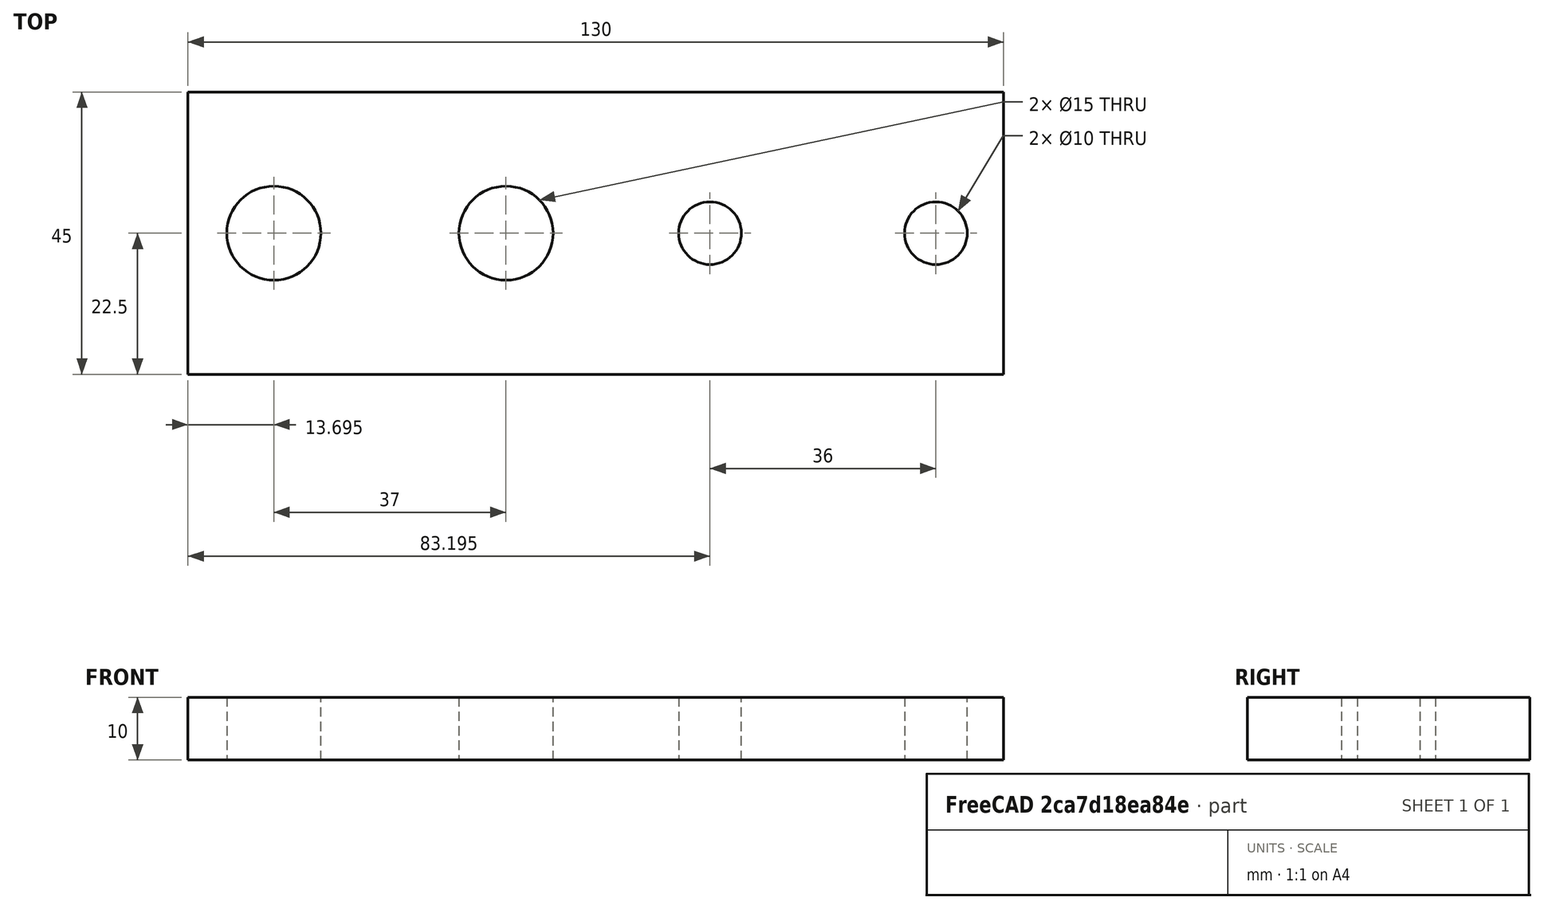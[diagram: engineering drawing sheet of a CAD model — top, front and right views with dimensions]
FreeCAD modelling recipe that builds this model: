
FCSTD DOCUMENT  (FreeCAD 2024.409R38991 (Git))
Label: SkadisMonkeyWrench
License: All rights reserved
LicenseURL: https://en.wikipedia.org/wiki/All_rights_reserved
objects: Sketcher::SketchObject×1, PartDesign::Pad×1, PartDesign::Body×1
note: 6 computed .brp shape members not serialized (recipe doc carries the construction recipe); baked Part::Feature solids carry a one-line shape summary decoded from their .brp

FEATURE [Sketcher::SketchObject] Sketch
  ArcFitTolerance = 1e-06
  AttachmentSupport = -> [XY_Plane]
  ExternalBSplineMaxDegree = 5
  ExternalBSplineTolerance = 0.0001
  FullyConstrained = false
  InternalTolerance = 1e-06
  InvalidShape = false
  MakeInternals = false
  MapMode = 5
  Support = -> [XY_Plane]
  TreeRank = 11
  ValidateShape = false
  sketch-geometry (12):
    g0: LineSegment StartX=0 StartY=0 StartZ=0 EndX=130 EndY=0 EndZ=0
    g1: LineSegment StartX=130 StartY=0 StartZ=0 EndX=130 EndY=45 EndZ=0
    g2: LineSegment StartX=130 StartY=45 StartZ=0 EndX=0 EndY=45 EndZ=0
    g3: LineSegment StartX=0 StartY=45 StartZ=0 EndX=0 EndY=0 EndZ=0
    g4: LineSegment [constr] StartX=0 StartY=22.5 StartZ=0 EndX=130 EndY=22.5 EndZ=0
    g5: Circle CenterX=13.6947 CenterY=22.5 CenterZ=0 NormalX=0 NormalY=0 NormalZ=1 AngleXU=0 Radius=7.5
    g6: Circle CenterX=50.6947 CenterY=22.5 CenterZ=0 NormalX=0 NormalY=0 NormalZ=1 AngleXU=0 Radius=7.5
    g7: Circle [constr] CenterX=32.1947 CenterY=22.5 CenterZ=0 NormalX=0 NormalY=0 NormalZ=1 AngleXU=0 Radius=11
    g8: Circle [constr] CenterX=68.1947 CenterY=22.5 CenterZ=0 NormalX=0 NormalY=0 NormalZ=1 AngleXU=0 Radius=10
    g9: Circle CenterX=83.1947 CenterY=22.5 CenterZ=0 NormalX=0 NormalY=0 NormalZ=1 AngleXU=0 Radius=5
    g10: Circle [constr] CenterX=101.195 CenterY=22.5 CenterZ=0 NormalX=0 NormalY=0 NormalZ=1 AngleXU=0 Radius=13
    g11: Circle CenterX=119.195 CenterY=22.5 CenterZ=0 NormalX=0 NormalY=0 NormalZ=1 AngleXU=0 Radius=5
  constraints (35):
    c: Coincident(g0,g1)
    c: Coincident(g1,g2)
    c: Coincident(g2,g3)
    c: Coincident(g3,g0)
    c: Horizontal(g0)
    c: Horizontal(g2)
    c: Vertical(g3)
    c: Coincident(g0,g-1)
    c: DistanceX(g0,g0) = 130
    c: DistanceY(g3,g3) = 45
    c: PointOnObject(g4,g3)
    c: PointOnObject(g4,g1)
    c: Horizontal(g4)
    c: DistanceY(g0,g4) = 22.5
    c: PointOnObject(g5,g4)
    c: Diameter(g5) = 15
    c: PointOnObject(g6,g4)
    c: Diameter(g6) = 15
    c: Diameter(g7) = 22
    c: Tangent(g5,g7)
    c: Tangent(g7,g6)
    c: PointOnObject(g8,g4)
    c: Tangent(g6,g8)
    c: PointOnObject(g9,g4)
    c: Diameter(g9) = 10
    c: Tangent(g9,g8)
    c: PointOnObject(g10,g4)
    c: Tangent(g9,g10)
    c: PointOnObject(g11,g4)
    c: Diameter(g11) = 10
    c: PointOnObject(g7,g4)
    c: Tangent(g11,g10)
    c: Diameter(g8) = 20
    c: Diameter(g10) = 26
    c: Equal(g0,g2)
FEATURE [PartDesign::Pad] Pad
  AddSubType = 0
  AlongSketchNormal = false
  AutoTaperInnerAngle = true
  CheckUpToFaceLimits = true
  ClaimChildren = false
  Direction = (0,0,1)
  Fit = 0
  FitJoin = 0
  InnerFit = 0
  InnerFitJoin = 0
  InvalidShape = false
  Length = 10
  Length2 = 10
  Linearize = true
  NewSolid = false
  Profile = -> Sketch
  ReferenceAxis = -> Sketch [N_Axis]
  Suppress = false
  TaperInnerAngle = 0
  TaperInnerAngleRev = 0
  TreeRank = 12
  Type = 0
  ValidateShape = true
  _ProfileBasedVersion = 1
FEATURE [PartDesign::Body] Body
  AutoGroupSolids = false
  ClaimAllChildren = false
  ExportMode = 0
  Group = -> [Sketch,Pad]
  InvalidShape = false
  Origin = -> Origin
  Tip = -> Pad
  TreeRank = 13
  ValidateShape = false
  _ExportChildren = -> [Pad]
  _GroupVersion = 1
